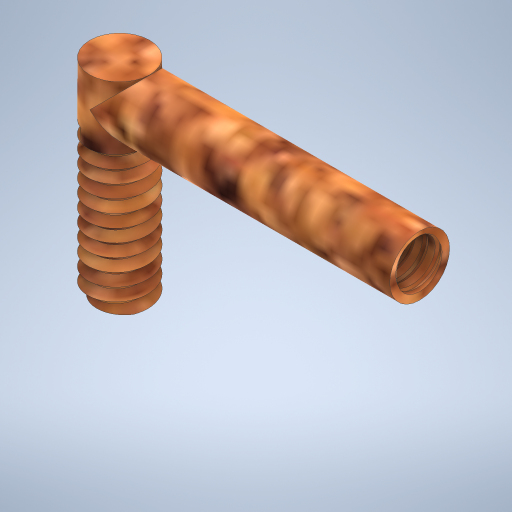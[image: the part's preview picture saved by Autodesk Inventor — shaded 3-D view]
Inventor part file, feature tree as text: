
AUTODESK INVENTOR PART (.ipt)
format: ipt  version: 2024 (Build 280153020, 153B)  size: 883,200 bytes
history: native  units: mm
features: sketch x5, extrude x3, helix x2, plane x1
ambient origin geometry x8: Origin, YZ Plane, XZ Plane, XY Plane, X Axis, Y Axis, Z Axis, Center Point
bodies: Solid1 (feature_tree)
feature tree (11):
  extrude  "Extrusion1"  Depth=1.7mm TaperAngle=0.0deg
  helix  "Coil1"  [1 undecoded]
  extrude  "Extrusion2"  Depth=0.2mm
  extrude  "Extrusion3"  Depth=1.7mm
  plane  "Work Plane1"
  helix  "Coil2"  [1 undecoded]
  sketch  "Sketch1"  dims[d0=8.0mm d1=27.0mm d2=0.0mm d3=1.7mm]
  sketch  "Sketch2"  dims[d4=60.0deg d5=0.2mm]
  sketch  "Sketch4"  dims[d6=2.0mm]
  sketch  "Sketch5"  dims[d7=1.7mm d8=22.0mm d9=10.0mm d10=0.0mm d11=90.0deg d12=90.0deg d13=0.0mm d14=0.0mm d15=8.0mm d16=40.0mm d17=0.0mm]
  sketch  "Sketch7"  dims[d18=6.0mm d19=25.0mm d20=0.0mm d28=23.0mm d29=1.7mm d30=60.0deg d31=2.2mm d32=2.0mm d33=0.2mm d34=1.7mm d35=27.0mm d36=10.0mm d37=0.0mm d38=90.0deg d39=90.0deg d40=0.0mm d41=0.0mm]
note: 2 required parameter values undecoded (feature->parameter linkage not recoverable at this tier; creation-order binding heuristic only, values carry confidence <= 0.55)
